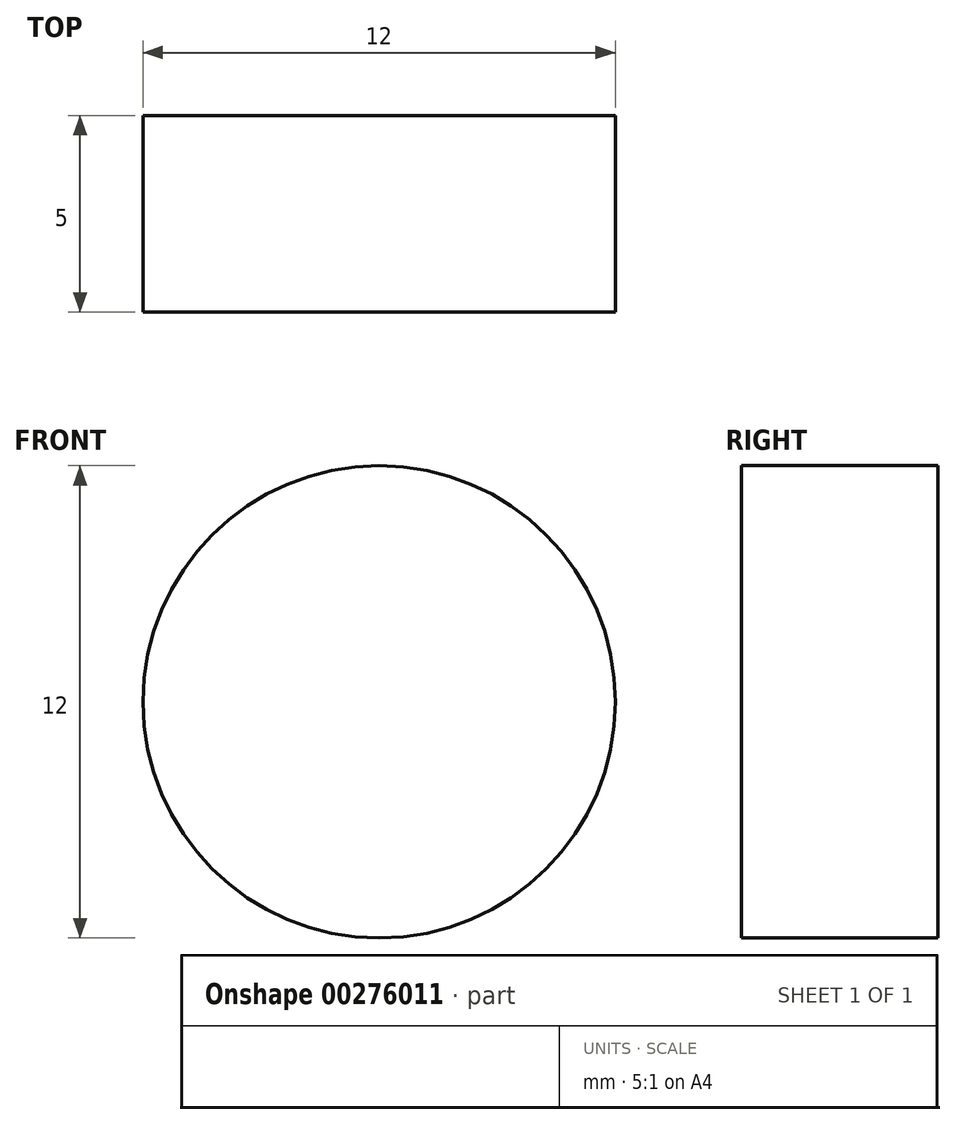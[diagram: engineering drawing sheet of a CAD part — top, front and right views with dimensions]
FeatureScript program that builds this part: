
annotation { "Feature Type Name" : "Feature", "Feature Type Description" : "" }
export const myFeature = defineFeature(function(context is Context, id is Id, definition is map)
    precondition{}
    {
        {
            var Q0;
            Q0=qCreatedBy(makeId("Front.planeOp"),FACE);
            var sketch = newSketch(context, id + "F0", { "sketchPlane" : qUnion([Q0])});
            skCircle(sketch, "E0", {"center": v(0, 0) * mm, "radius": 120 * mm});
            skCircle(sketch, "E1", {"center": v(0, 0) * mm, "radius": 115 * mm});
            skSolve(sketch);
        }
        {
            var Q0;
            Q0=makeQuery(id+"F0.imprint","IMPRINT",FACE,{"disambiguationData":[TD([[makeQuery(id+"F0.imprint","IMPRINT",EDGE,{"derivedFrom":sQuery(id+"F0.wireOp",EDGE,"E0")}),1.0]])]});
            extrude(context, id + "F1", {"entities" : qUnion([Q0]), "endBound" : BoundingType.SYMMETRIC, "depth" : 110 * mm});
        }
        {
            var Q0;
            Q0=makeQuery(id+"F1.opExtrude","CAP_FACE",FACE,{"disambiguationData":[OSD([sQuery(id+"F0.wireOp",EDGE,"E0"),sQuery(id+"F0.wireOp",EDGE,"E1")])],"isStart":true});
            var sketch = newSketch(context, id + "F2", { "sketchPlane" : qUnion([Q0])});
            skArc(sketch, "E2", {"start": v(75, -129.9) * mm, "mid": v(150, 0) * mm, "end": v(75, 129.9) * mm});
            skLineSegment(sketch, "E3", {"start": v(0, 0) * mm, "end": v(75, 129.9) * mm});
            skLineSegment(sketch, "E4", {"start": v(0, 0) * mm, "end": v(75, -129.9) * mm});
            skSolve(sketch);
        }
        {
            var Q0;
            {var subQ0=sQuery(id+"F2.wireOp",EDGE,"E2");Q0=makeQuery(id+"F2.imprint","IMPRINT",FACE,{"disambiguationData":[TD([[makeQuery(id+"F2.imprint","IMPRINT",EDGE,{"derivedFrom":subQ0}),1.0]])]});}
            extrude(context, id + "F3", {"entities" : qUnion([Q0]), "operationType" : NewBodyOperationType.ADD, "oppositeDirection" : true, "depth" : 5 * mm});
        }
        {
            var Q0;
            {var subQ0=sQuery(id+"F0.wireOp",EDGE,"E0");Q0=makeQuery(id+"F3.boolean.opBoolean","MERGE",FACE,{"derivedFrom":[makeQuery(id+"F1.opExtrude","CAP_FACE",FACE,{"disambiguationData":[OSD([subQ0,sQuery(id+"F0.wireOp",EDGE,"E1")])],"isStart":true}),makeQuery(id+"F3.opExtrude","CAP_FACE",FACE,{"disambiguationData":[OSD([subQ0,sQuery(id+"F2.wireOp",EDGE,"E2"),sQuery(id+"F2.wireOp",EDGE,"E3"),sQuery(id+"F2.wireOp",EDGE,"E4")])],"isStart":true})]});}
            var sketch = newSketch(context, id + "F4", { "sketchPlane" : qUnion([Q0])});
            skCircle(sketch, "E5", {"center": v(0, 0) * mm, "radius": 135 * mm});
            skCircle(sketch, "E6", {"center": v(135, 0) * mm, "radius": 6 * mm});
            skSolve(sketch);
        }
        {
            var Q0;
            {var subQ0=sQuery(id+"F4.wireOp",EDGE,"E6");var subQ1=sQuery(id+"F4.wireOp",EDGE,"E5");var subQ2=makeQuery(id+"F4.imprint","INTERSECT",VERTEX,{"disambiguationData":[OD(0.0)],"derivedFrom":[subQ1,subQ0]});Q0=makeQuery(id+"F4.imprint","IMPRINT",FACE,{"disambiguationData":[TD([[makeQuery(id+"F4.imprint","IMPRINT",EDGE,{"disambiguationData":[TD([[subQ2,1.0]])],"derivedFrom":subQ1}),-1.0]])]});}
            var Q1;
            {var subQ0=sQuery(id+"F4.wireOp",EDGE,"E6");var subQ1=sQuery(id+"F4.wireOp",EDGE,"E5");var subQ2=makeQuery(id+"F4.imprint","INTERSECT",VERTEX,{"disambiguationData":[OD(0.0)],"derivedFrom":[subQ1,subQ0]});Q1=makeQuery(id+"F4.imprint","IMPRINT",FACE,{"disambiguationData":[TD([[makeQuery(id+"F4.imprint","IMPRINT",EDGE,{"disambiguationData":[TD([[subQ2,1.0]])],"derivedFrom":subQ1}),1.0]])]});}
            extrude(context, id + "F5", {"entities" : qUnion([Q0, Q1]), "operationType" : NewBodyOperationType.REMOVE, "endBound" : BoundingType.THROUGH_ALL, "oppositeDirection" : true, "depth" : 25.4 * mm});
        }
        {
            var Q0;
            Q0=qCreatedBy(makeId("Right.planeOp"),FACE);
            var sketch = newSketch(context, id + "F6", { "sketchPlane" : qUnion([Q0])});
            skCircle(sketch, "E7", {"center": v(0, 0) * mm, "radius": 6.35 * mm});
            skSolve(sketch);
        }
        {
            var Q0;
            Q0=makeQuery(id+"F6.imprint","IMPRINT",FACE,{"disambiguationData":[TD([[makeQuery(id+"F6.imprint","IMPRINT",EDGE,{"derivedFrom":sQuery(id+"F6.wireOp",EDGE,"E7")}),1.0]])]});
            extrude(context, id + "F7", {"entities" : qUnion([Q0]), "operationType" : NewBodyOperationType.REMOVE, "endBound" : BoundingType.SYMMETRIC, "oppositeDirection" : true, "depth" : 508 * mm});
        }
    });
